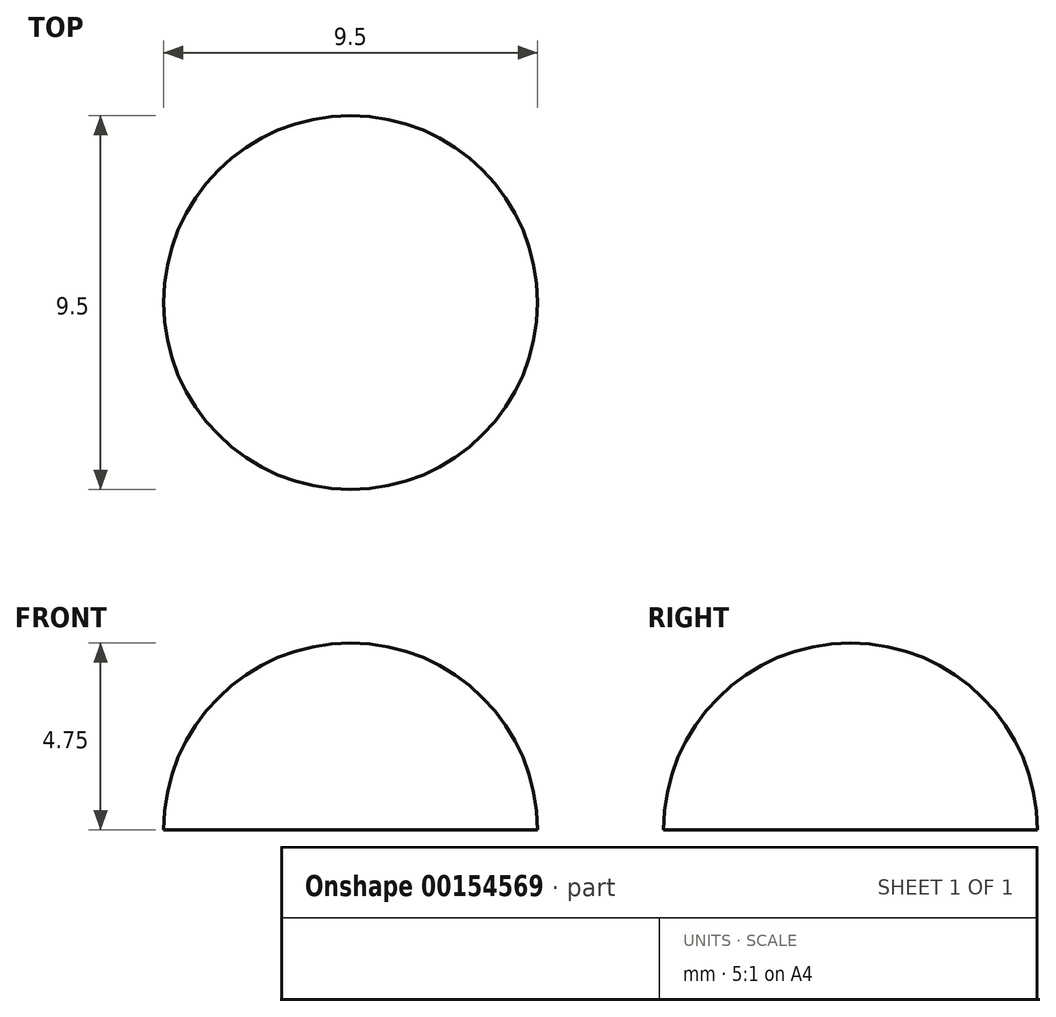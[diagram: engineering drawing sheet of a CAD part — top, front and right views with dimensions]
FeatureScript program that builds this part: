
annotation { "Feature Type Name" : "Feature", "Feature Type Description" : "" }
export const myFeature = defineFeature(function(context is Context, id is Id, definition is map)
    precondition{}
    {
        {
            var Q0;
            Q0=qCreatedBy(makeId("Top.planeOp"),FACE);
            var sketch = newSketch(context, id + "F0", { "sketchPlane" : qUnion([Q0])});
            skLineSegment(sketch, "E0", {"start": v(-4.75, 0) * mm, "end": v(4.75, 0) * mm});
            skArc(sketch, "E1", {"start": v(4.75, 0) * mm, "mid": v(0, 4.75) * mm, "end": v(-4.75, 0) * mm});
            skSolve(sketch);
        }
        {
            var Q0;
            Q0 = qSketchRegion(id + "F0", true);
            var Q1;
            Q1=sQuery(id+"F0.wireOp",EDGE,"E0");
            revolve(context, id + "F1", {"entities" : qUnion([Q0]), "axis" : qUnion([Q1]), "revolveType" : RevolveType.ONE_DIRECTION, "angle" : 180 * degree});
        }
    });
